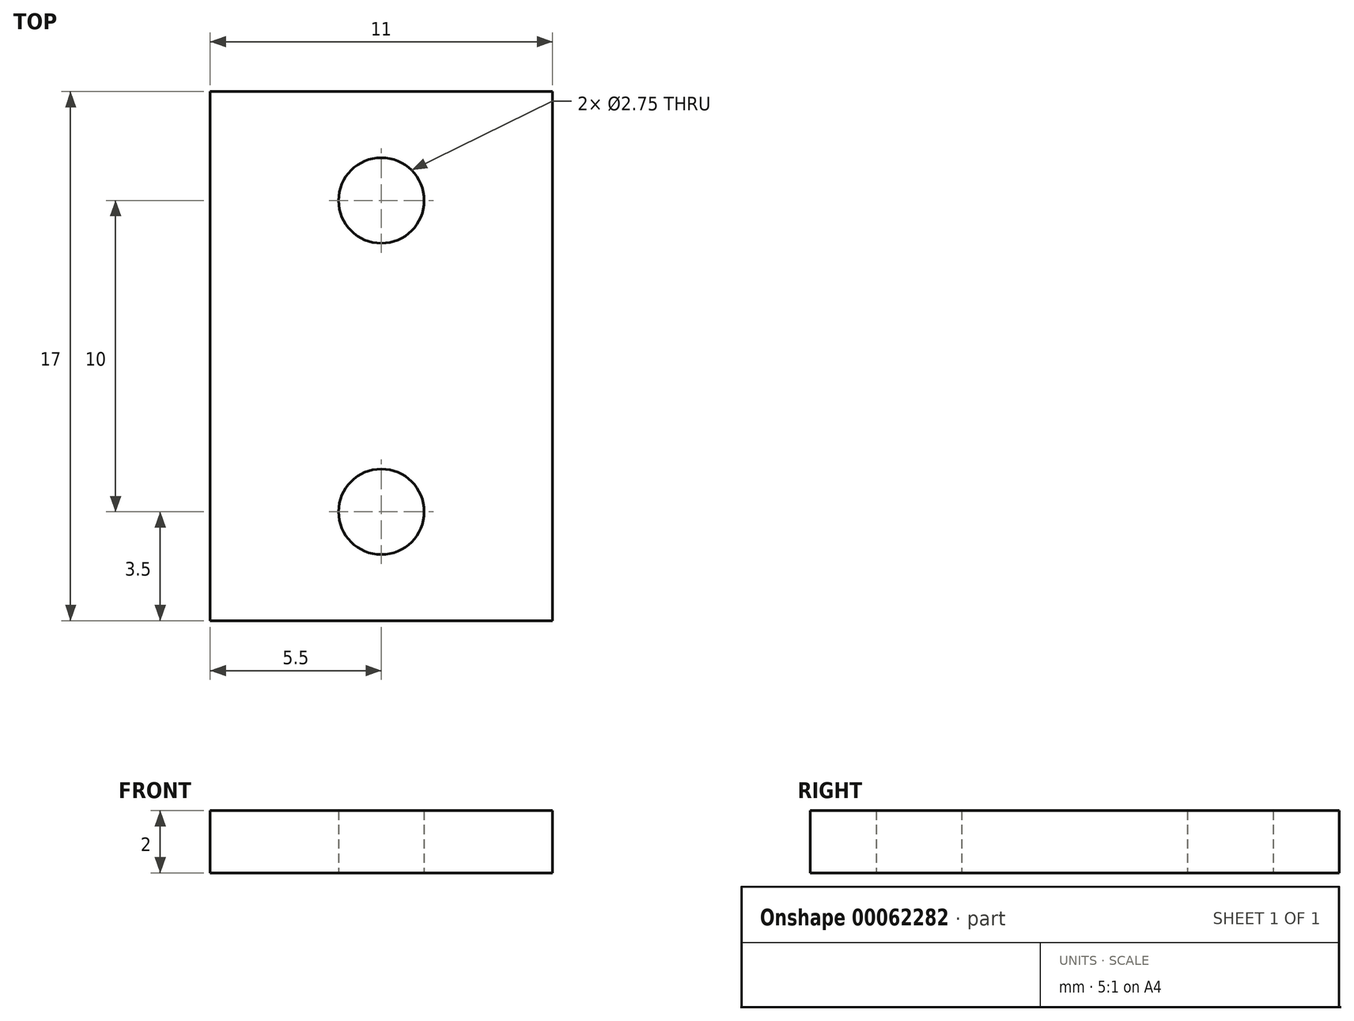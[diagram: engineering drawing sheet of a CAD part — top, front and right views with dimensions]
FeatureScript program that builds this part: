
annotation { "Feature Type Name" : "Feature", "Feature Type Description" : "" }
export const myFeature = defineFeature(function(context is Context, id is Id, definition is map)
    precondition{}
    {
        {
            var Q0;
            Q0=qCreatedBy(makeId("Top.planeOp"),FACE);
            var sketch = newSketch(context, id + "F0", { "sketchPlane" : qUnion([Q0])});
            skLineSegment(sketch, "E0.rect.bottom", {"start": v(-5.5, -8.5) * mm, "end": v(5.5, -8.5) * mm});
            skLineSegment(sketch, "E0.rect.top", {"start": v(-5.5, 8.5) * mm, "end": v(5.5, 8.5) * mm});
            skLineSegment(sketch, "E0.rect.left", {"start": v(-5.5, -8.5) * mm, "end": v(-5.5, 8.5) * mm});
            skLineSegment(sketch, "E0.rect.right", {"start": v(5.5, -8.5) * mm, "end": v(5.5, 8.5) * mm});
            skPoint(sketch, "E0.rect.middle", {"position": v(0, 0) * mm});
            skCircle(sketch, "E1", {"center": v(0, 5) * mm, "radius": 1.38 * mm});
            skCircle(sketch, "E2.MirrorC", {"center": v(0, -5) * mm, "radius": 1.38 * mm});
            skSolve(sketch);
        }
        {
            var Q0;
            Q0 = qSketchRegion(id + "F0", true);
            extrude(context, id + "F1", {"entities" : qUnion([Q0]), "depth" : 2 * mm});
        }
    });
